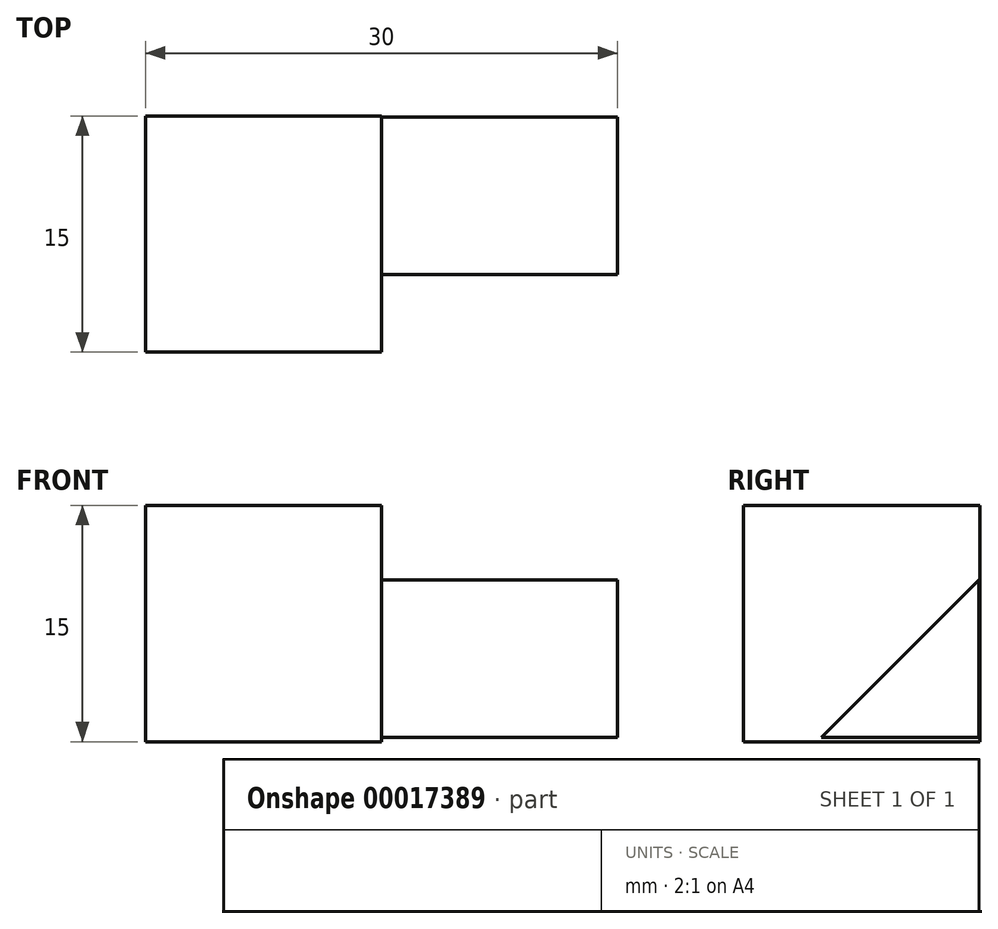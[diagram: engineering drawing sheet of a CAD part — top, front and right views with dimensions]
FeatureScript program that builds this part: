
annotation { "Feature Type Name" : "Feature", "Feature Type Description" : "" }
export const myFeature = defineFeature(function(context is Context, id is Id, definition is map)
    precondition{}
    {
        {
            var Q0;
            Q0=qCreatedBy(makeId("Right.planeOp"),FACE);
            var sketch = newSketch(context, id + "F0", { "sketchPlane" : qUnion([Q0])});
            skLineSegment(sketch, "E0.bottom", {"start": v(-6.01, 3.68) * mm, "end": v(8.99, 3.68) * mm});
            skLineSegment(sketch, "E0.top", {"start": v(-6.01, 18.68) * mm, "end": v(8.99, 18.68) * mm});
            skLineSegment(sketch, "E0.left", {"start": v(-6.01, 3.68) * mm, "end": v(-6.01, 18.68) * mm});
            skLineSegment(sketch, "E0.right", {"start": v(8.99, 3.68) * mm, "end": v(8.99, 18.68) * mm});
            skSolve(sketch);
        }
        {
            var Q0;
            Q0=qCreatedBy(makeId("Right.planeOp"),FACE);
            var sketch = newSketch(context, id + "F1", { "sketchPlane" : qUnion([Q0])});
            skLineSegment(sketch, "E1", {"start": v(8.92, 3.94) * mm, "end": v(8.92, 13.94) * mm});
            skLineSegment(sketch, "E2", {"start": v(8.92, 13.94) * mm, "end": v(-1.08, 3.94) * mm});
            skLineSegment(sketch, "E3", {"start": v(-1.08, 3.94) * mm, "end": v(8.92, 3.94) * mm});
            skSolve(sketch);
        }
        {
            var Q0;
            Q0=makeQuery(id+"F1.imprint","IMPRINT",FACE,{"disambiguationData":[TD([[makeQuery(id+"F1.imprint","IMPRINT",EDGE,{"derivedFrom":sQuery(id+"F1.wireOp",EDGE,"E1")}),1.0]])]});
            extrude(context, id + "F2", {"entities" : qUnion([Q0]), "depth" : 15 * mm});
        }
        {
            var Q0;
            Q0=makeQuery(id+"F0.imprint","IMPRINT",FACE,{"disambiguationData":[TD([[makeQuery(id+"F0.imprint","IMPRINT",EDGE,{"derivedFrom":sQuery(id+"F0.wireOp",EDGE,"E0.bottom")}),1.0]])]});
            extrude(context, id + "F3", {"entities" : qUnion([Q0]), "operationType" : NewBodyOperationType.ADD, "oppositeDirection" : true, "depth" : 15 * mm});
        }
    });
